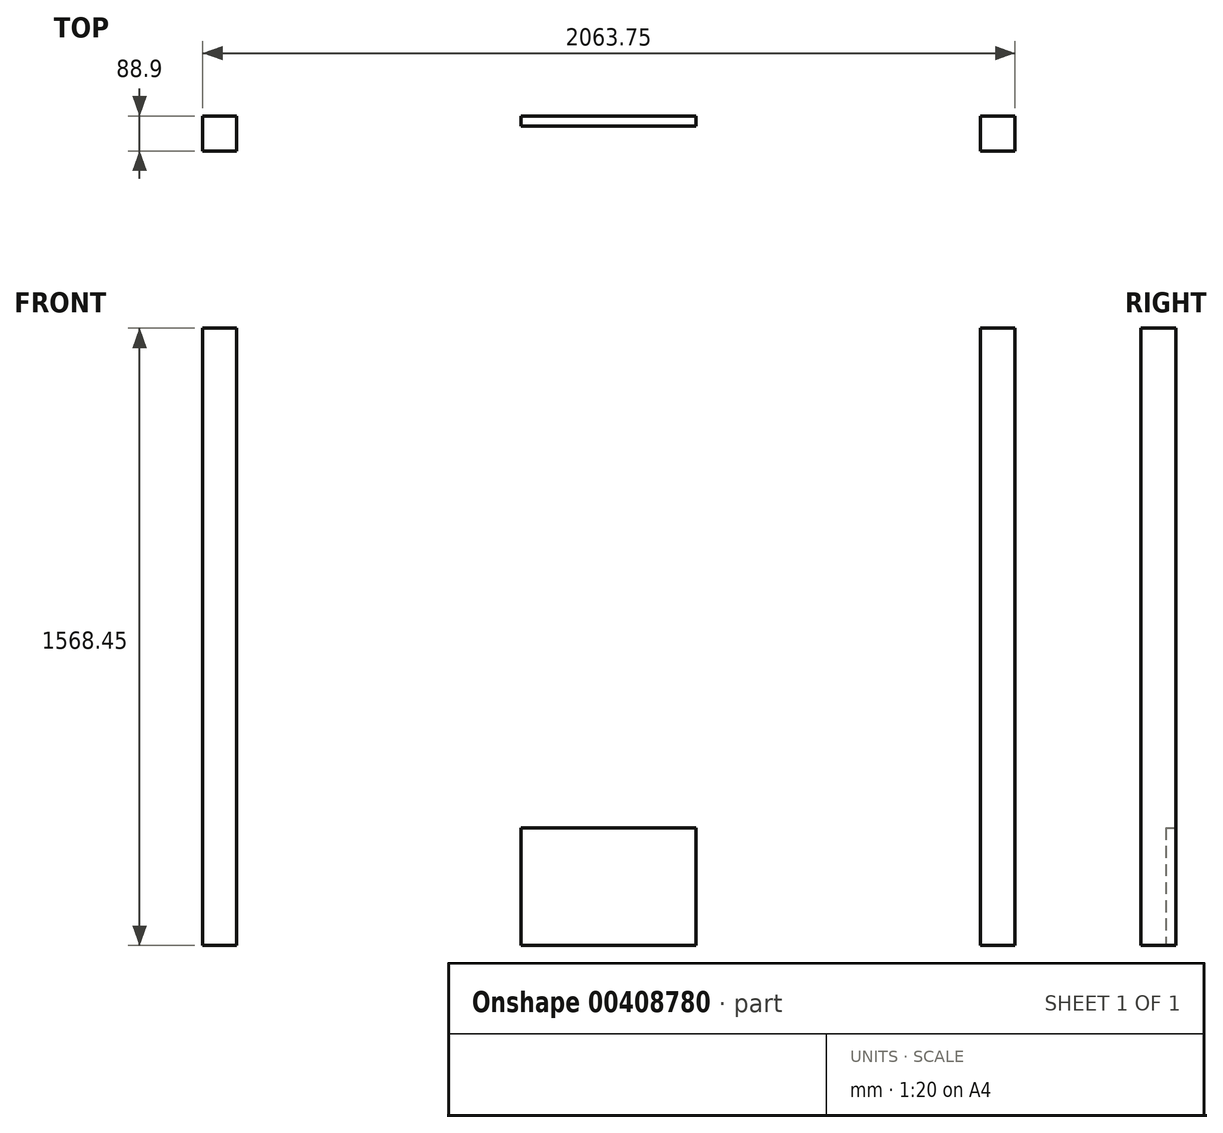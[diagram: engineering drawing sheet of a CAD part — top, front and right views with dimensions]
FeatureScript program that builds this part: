
annotation { "Feature Type Name" : "Feature", "Feature Type Description" : "" }
export const myFeature = defineFeature(function(context is Context, id is Id, definition is map)
    precondition{}
    {
        {
            var Q0;
            Q0=qCreatedBy(makeId("Front.planeOp"),FACE);
            var sketch = newSketch(context, id + "F0", { "sketchPlane" : qUnion([Q0])});
            skLineSegment(sketch, "E0.bottom", {"start": v(-1031.08, 0) * mm, "end": v(-945.36, 0) * mm});
            skLineSegment(sketch, "E0.top", {"start": v(-1031.08, 1270) * mm, "end": v(-945.36, 1270) * mm});
            skLineSegment(sketch, "E0.left", {"start": v(-1031.08, 0) * mm, "end": v(-1031.08, 1270) * mm});
            skLineSegment(sketch, "E0.right", {"start": v(-945.36, 0) * mm, "end": v(-945.36, 1270) * mm});
            skLineSegment(sketch, "E1.bottom", {"start": v(945.36, 0) * mm, "end": v(1032.67, 0) * mm, "construction": true});
            skLineSegment(sketch, "E1.top", {"start": v(945.36, 1270) * mm, "end": v(1032.67, 1270) * mm});
            skLineSegment(sketch, "E1.left", {"start": v(945.36, 0) * mm, "end": v(945.36, 1270) * mm});
            skLineSegment(sketch, "E1.right", {"start": v(1032.67, 0) * mm, "end": v(1032.67, 1270) * mm});
            skLineSegment(sketch, "E2", {"start": v(-945.36, 0) * mm, "end": v(945.36, 0) * mm, "construction": true});
            skLineSegment(sketch, "E3.bottom", {"start": v(-1031.08, 0) * mm, "end": v(-945.36, 0) * mm, "construction": true});
            skLineSegment(sketch, "E3.top", {"start": v(-1031.08, -298.45) * mm, "end": v(-945.36, -298.45) * mm});
            skLineSegment(sketch, "E3.left", {"start": v(-1031.08, 0) * mm, "end": v(-1031.08, -298.45) * mm});
            skLineSegment(sketch, "E3.right", {"start": v(-945.36, 0) * mm, "end": v(-945.36, -298.45) * mm});
            skLineSegment(sketch, "E4.bottom", {"start": v(945.36, 0) * mm, "end": v(1032.67, 0) * mm});
            skLineSegment(sketch, "E4.top", {"start": v(945.36, -298.45) * mm, "end": v(1032.67, -298.45) * mm});
            skLineSegment(sketch, "E4.left", {"start": v(945.36, 0) * mm, "end": v(945.36, -298.45) * mm});
            skLineSegment(sketch, "E4.right", {"start": v(1032.67, 0) * mm, "end": v(1032.67, -298.45) * mm});
            skSolve(sketch);
        }
        {
            var Q0;
            Q0 = qSketchRegion(id + "F0", true);
            extrude(context, id + "F1", {"entities" : qUnion([Q0]), "depth" : 88.9 * mm});
        }
        {
            var Q0;
            Q0=qCreatedBy(makeId("Front.planeOp"),FACE);
            var sketch = newSketch(context, id + "F2", { "sketchPlane" : qUnion([Q0])});
            skLineSegment(sketch, "E5.bottom", {"start": v(-222.25, 0) * mm, "end": v(222.25, 0) * mm});
            skLineSegment(sketch, "E5.top", {"start": v(-222.25, -298.45) * mm, "end": v(222.25, -298.45) * mm});
            skLineSegment(sketch, "E5.left", {"start": v(-222.25, 0) * mm, "end": v(-222.25, -298.45) * mm});
            skLineSegment(sketch, "E5.right", {"start": v(222.25, 0) * mm, "end": v(222.25, -298.45) * mm});
            skSolve(sketch);
        }
        {
            var Q0;
            Q0 = qSketchRegion(id + "F2", true);
            extrude(context, id + "F3", {"entities" : qUnion([Q0]), "depth" : 25.4 * mm});
        }
    });
